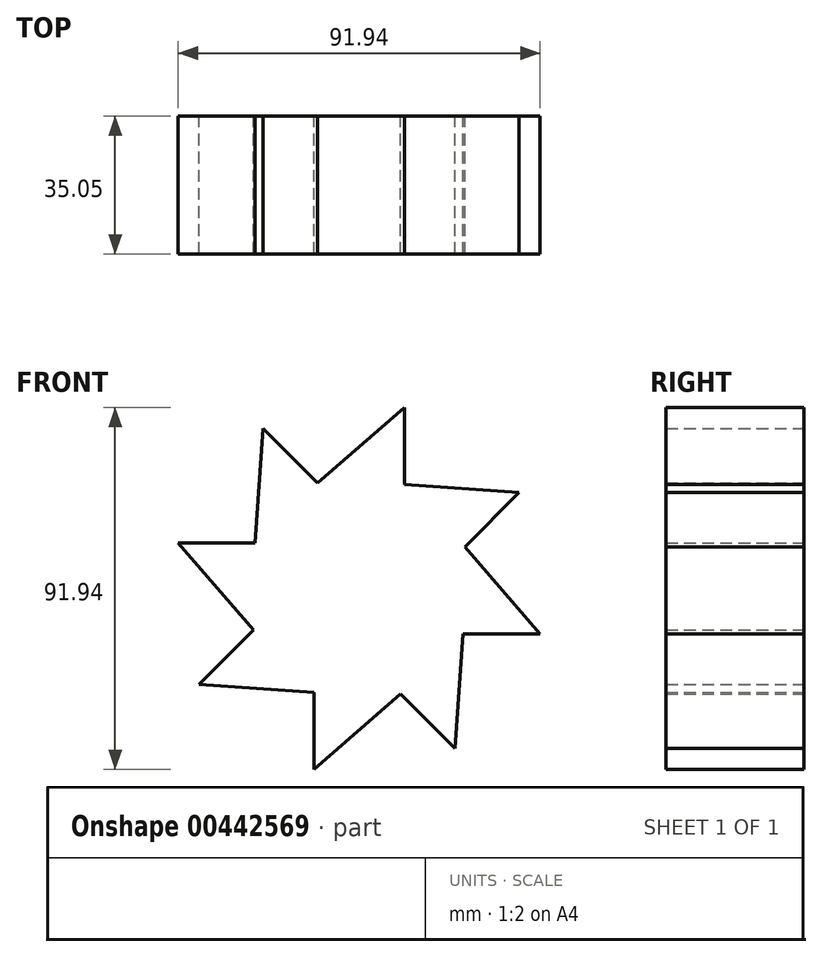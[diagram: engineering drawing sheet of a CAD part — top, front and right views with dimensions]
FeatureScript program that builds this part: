
annotation { "Feature Type Name" : "Feature", "Feature Type Description" : "" }
export const myFeature = defineFeature(function(context is Context, id is Id, definition is map)
    precondition{}
    {
        {
            var Q0;
            Q0=qCreatedBy(makeId("Front.planeOp"),FACE);
            var sketch = newSketch(context, id + "F0", { "sketchPlane" : qUnion([Q0])});
            skLineSegment(sketch, "E0", {"start": v(-10.54, 26.83) * mm, "end": v(11.52, 45.97) * mm});
            skLineSegment(sketch, "E1", {"start": v(11.52, 45.97) * mm, "end": v(11.52, 26.43) * mm});
            skLineSegment(sketch, "E2.1.0", {"start": v(-26.43, 11.52) * mm, "end": v(-24.36, 40.65) * mm});
            skLineSegment(sketch, "E2.1.1", {"start": v(-24.36, 40.65) * mm, "end": v(-10.54, 26.83) * mm});
            skLineSegment(sketch, "E2.2.0", {"start": v(-26.83, -10.54) * mm, "end": v(-45.97, 11.52) * mm});
            skLineSegment(sketch, "E2.2.1", {"start": v(-45.97, 11.52) * mm, "end": v(-26.43, 11.52) * mm});
            skLineSegment(sketch, "E2.3.0", {"start": v(-11.52, -26.43) * mm, "end": v(-40.65, -24.36) * mm});
            skLineSegment(sketch, "E2.3.1", {"start": v(-40.65, -24.36) * mm, "end": v(-26.83, -10.54) * mm});
            skLineSegment(sketch, "E2.4.0", {"start": v(10.54, -26.83) * mm, "end": v(-11.52, -45.97) * mm});
            skLineSegment(sketch, "E2.4.1", {"start": v(-11.52, -45.97) * mm, "end": v(-11.52, -26.43) * mm});
            skLineSegment(sketch, "E2.5.0", {"start": v(26.43, -11.52) * mm, "end": v(24.36, -40.65) * mm});
            skLineSegment(sketch, "E2.5.1", {"start": v(24.36, -40.65) * mm, "end": v(10.54, -26.83) * mm});
            skLineSegment(sketch, "E2.6.0", {"start": v(26.83, 10.54) * mm, "end": v(45.97, -11.52) * mm});
            skLineSegment(sketch, "E2.6.1", {"start": v(45.97, -11.52) * mm, "end": v(26.43, -11.52) * mm});
            skLineSegment(sketch, "E2.7.0", {"start": v(11.52, 26.43) * mm, "end": v(40.65, 24.36) * mm});
            skLineSegment(sketch, "E2.7.1", {"start": v(40.65, 24.36) * mm, "end": v(26.83, 10.54) * mm});
            skPoint(sketch, "E2.center", {"position": v(0, 0) * mm});
            skSolve(sketch);
        }
        {
            var Q0;
            Q0=makeQuery(id+"F0.imprint","IMPRINT",FACE,{"disambiguationData":[TD([[makeQuery(id+"F0.imprint","IMPRINT",EDGE,{"derivedFrom":sQuery(id+"F0.wireOp",EDGE,"E0")}),-1.0]])]});
            extrude(context, id + "F1", {"entities" : qUnion([Q0]), "depth" : 35.05 * mm});
        }
    });
